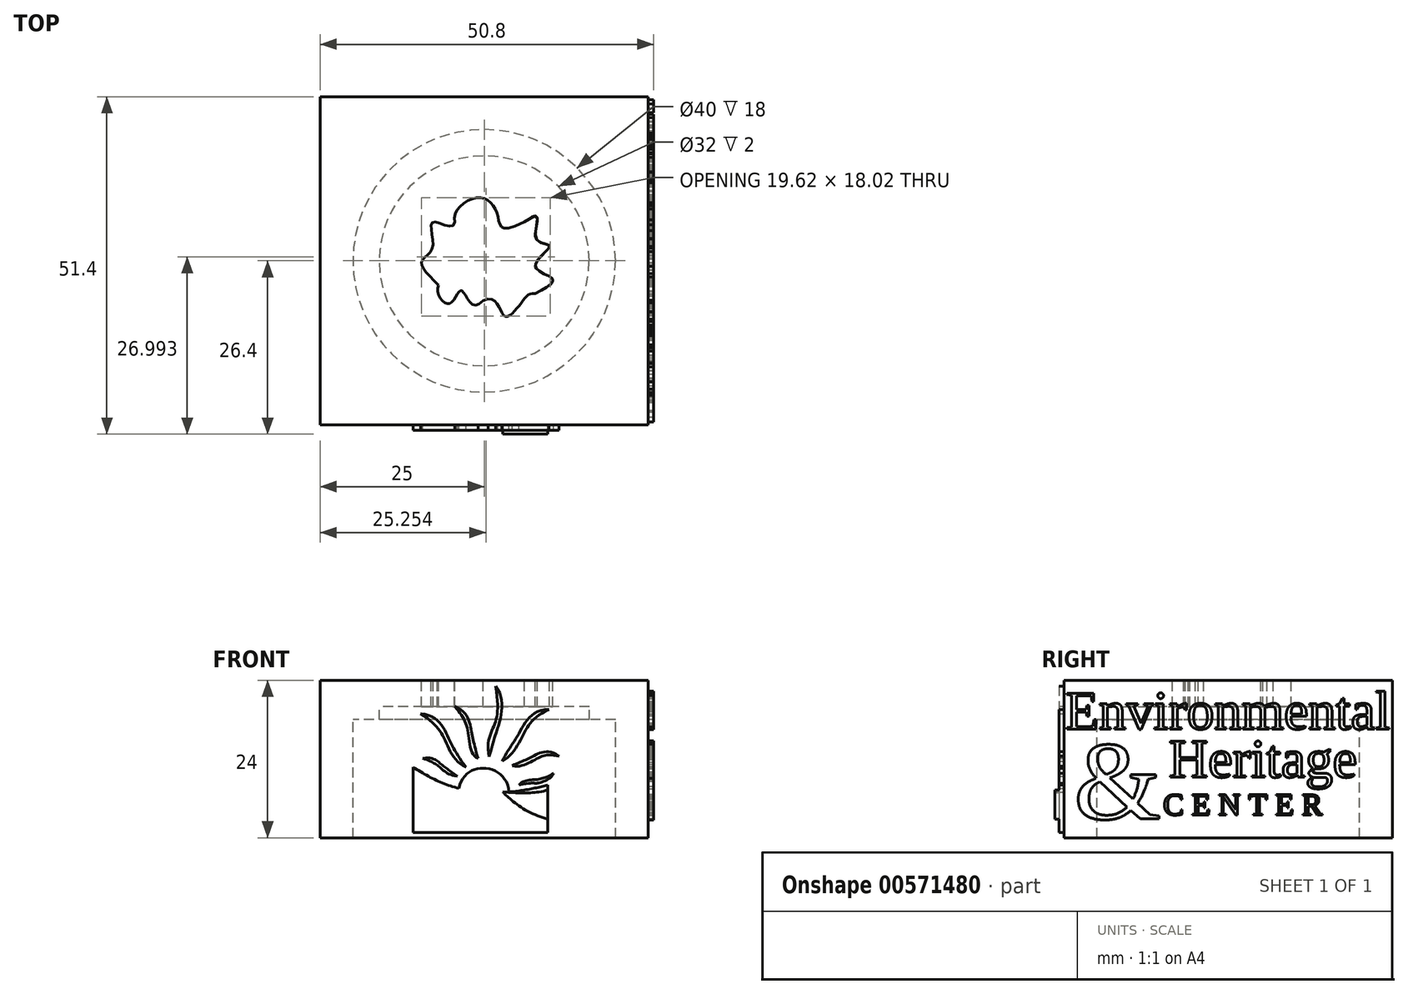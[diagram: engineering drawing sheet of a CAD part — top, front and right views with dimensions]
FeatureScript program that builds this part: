
annotation { "Feature Type Name" : "Feature", "Feature Type Description" : "" }
export const myFeature = defineFeature(function(context is Context, id is Id, definition is map)
    precondition{}
    {
        {
            var Q0;
            Q0=qCreatedBy(makeId("Top.planeOp"),FACE);
            var Q1;
            Q1=qBodyType(qCreatedBy(id+"F1",EDGE),BodyType.WIRE);
            cPlane(context, id + "F0", {"entities" : qUnion([Q0, Q1]), "cplaneType" : CPlaneType.OFFSET, "offset" : 12 * mm, "width" : 150 * mm, "height" : 150 * mm});
        }
        {
            var Q0;
            Q0=qCreatedBy(id+"F0.planeOp",FACE);
            var sketch = newSketch(context, id + "F1", { "sketchPlane" : qUnion([Q0])});
            skCircle(sketch, "E0", {"center": v(0, 0) * mm, "radius": 22 * mm});
            skCircle(sketch, "E1", {"center": v(0, 0) * mm, "radius": 20 * mm});
            skLineSegment(sketch, "E2.bottom", {"start": v(-25, 25) * mm, "end": v(25, 25) * mm});
            skLineSegment(sketch, "E2.top", {"start": v(-25, -25) * mm, "end": v(25, -25) * mm});
            skLineSegment(sketch, "E2.left", {"start": v(-25, 25) * mm, "end": v(-25, -25) * mm});
            skLineSegment(sketch, "E2.right", {"start": v(25, 25) * mm, "end": v(25, -25) * mm});
            skFitSpline(sketch, "E3", {"points": [v(6.14, 5.9) * mm, v(2.03, 7.03) * mm, v(-1.07, 9.6) * mm, v(-4.49, 5.9) * mm], "startDerivative": vector(-37.97, -19.2) * mm, "endDerivative": vector(4.73, -13.73) * mm});
            skFitSpline(sketch, "E4", {"points": [v(-4.49, 5.9) * mm, v(-7.75, 5.9) * mm, v(-7.85, 2.06) * mm, v(-9.5, -0.02) * mm, v(-6.95, -3.7) * mm], "startDerivative": vector(-0.77, -19.25) * mm, "endDerivative": vector(17.43, -16.5) * mm});
            skFitSpline(sketch, "E5", {"points": [v(-6.95, -3.7) * mm, v(-5.34, -6.54) * mm, v(-3.42, -4.56) * mm, v(-0.16, -6.05) * mm], "startDerivative": vector(-5.94, -10.16) * mm, "endDerivative": vector(15.66, 18.1) * mm});
            skFitSpline(sketch, "E6", {"points": [v(-0.16, -6.05) * mm, v(3.1, -8.4) * mm, v(5.82, -6.16) * mm, v(7.8, -4.99) * mm], "startDerivative": vector(18.56, 8.63) * mm, "endDerivative": vector(11.76, -0.42) * mm});
            skFitSpline(sketch, "E7", {"points": [v(7.8, -4.99) * mm, v(10.41, -2.8) * mm, v(7.8, -0.82) * mm, v(9.93, 2.28) * mm, v(7.8, 3.83) * mm, v(6.14, 5.9) * mm], "startDerivative": vector(20.8, 11.18) * mm, "endDerivative": vector(-51.3, -41.03) * mm});
            skSolve(sketch);
        }
        {
            var Q0;
            Q0=qCreatedBy(makeId("Top.planeOp"),FACE);
            cPlane(context, id + "F2", {"entities" : qUnion([Q0]), "cplaneType" : CPlaneType.OFFSET, "offset" : 8 * mm, "width" : 150 * mm, "height" : 150 * mm});
        }
        {
            var Q0;
            Q0=qCreatedBy(id+"F2.planeOp",FACE);
            var sketch = newSketch(context, id + "F3", { "sketchPlane" : qUnion([Q0])});
            skCircle(sketch, "E8", {"center": v(0, 0) * mm, "radius": 20 * mm});
            skCircle(sketch, "E9", {"center": v(0, 0) * mm, "radius": 16 * mm});
            skSolve(sketch);
        }
        {
            var Q0;
            Q0=makeQuery(id+"F1.imprint","IMPRINT",FACE,{"disambiguationData":[TD([[makeQuery(id+"F1.imprint","IMPRINT",EDGE,{"derivedFrom":sQuery(id+"F1.wireOp",EDGE,"E1")}),1.0]])]});
            extrude(context, id + "F4", {"entities" : qUnion([Q0]), "oppositeDirection" : true, "depth" : 4 * mm, "offsetDistance" : 25 * mm});
        }
        {
            var Q0;
            Q0=makeQuery(id+"F1.imprint","IMPRINT",FACE,{"disambiguationData":[TD([[makeQuery(id+"F1.imprint","IMPRINT",EDGE,{"derivedFrom":sQuery(id+"F1.wireOp",EDGE,"E0")}),1.0]])]});
            var Q1;
            Q1=makeQuery(id+"F1.imprint","IMPRINT",FACE,{"disambiguationData":[TD([[makeQuery(id+"F1.imprint","IMPRINT",EDGE,{"derivedFrom":sQuery(id+"F1.wireOp",EDGE,"E0")}),-1.0]])]});
            extrude(context, id + "F5", {"entities" : qUnion([Q0, Q1]), "operationType" : NewBodyOperationType.ADD, "oppositeDirection" : true, "depth" : 24 * mm, "offsetDistance" : 25 * mm});
        }
        {
            var Q0;
            Q0=makeQuery(id+"F3.imprint","IMPRINT",FACE,{"disambiguationData":[TD([[makeQuery(id+"F3.imprint","IMPRINT",EDGE,{"derivedFrom":sQuery(id+"F3.wireOp",EDGE,"E8")}),1.0]])]});
            extrude(context, id + "F6", {"entities" : qUnion([Q0]), "operationType" : NewBodyOperationType.ADD, "oppositeDirection" : true, "depth" : 2 * mm});
        }
        {
            var Q0;
            Q0=qCreatedBy(id+"F0.planeOp",FACE);
            var sketch = newSketch(context, id + "F7", { "sketchPlane" : qUnion([Q0])});
            skCircle(sketch, "E10", {"center": v(0, 0) * mm, "radius": 22.4 * mm});
            skSolve(sketch);
        }
        {
            var Q0;
            Q0=qSketchRegion(id+"F7",true);
            var Q1;
            Q1=qConstructionFilter(qBodyType(qCreatedBy(id+"F7",EDGE),BodyType.WIRE),ConstructionObject.NO);
            extrude(context, id + "F8", {"entities" : qUnion([Q0]), "bodyType" : ToolBodyType.SURFACE, "operationType" : NewBodyOperationType.ADD, "surfaceEntities" : qUnion([Q1]), "oppositeDirection" : true, "depth" : 24 * mm});
        }
        {
            var Q0;
            Q0=makeQuery(id+"F5.opExtrude","SWEPT_FACE",FACE,{"disambiguationData":[OSD([sQuery(id+"F1.wireOp",EDGE,"E2.right")])]});
            var sketch = newSketch(context, id + "F9", { "sketchPlane" : qUnion([Q0])});
            skText(sketch, "E11", { "text": "Environmental", "fontName": "Tinos-Regular.ttf"});
            skText(sketch, "E12", { "text": "Heritage", "fontName": "Tinos-Regular.ttf"});
            skText(sketch, "E13", { "text": "C E N T E R", "fontName": "Tinos-Regular.ttf"});
            skText(sketch, "E14", { "text": "&", "fontName": "Tinos-Regular.ttf"});
            const initialGuessF9  = {"E11": [-0.02481, 0.00457, 1, 0, 0.006], "E12": [-0.00905, -0.00277, 1, 0, 0.006], "E13": [-0.0099, -0.00853, 1, 0, 0.0034], "E14": [-0.0235, -0.00912, 1, 0, 0.0123]};
            skSetInitialGuess(sketch, initialGuessF9);
            skSolve(sketch);
        }
        {
            var Q0;
            Q0=qSketchRegion(id+"F9",true);
            var Q1;
            Q1=makeQuery(id+"F8.opExtrude","SWEPT_FACE",FACE,{"disambiguationData":[OSD([sQuery(id+"F7.wireOp",EDGE,"E10")])]});
            var Q2;
            Q2=makeQuery(id+"F5.opExtrude","SWEPT_FACE",FACE,{"disambiguationData":[OSD([sQuery(id+"F1.wireOp",EDGE,"E0")])]});
            extrude(context, id + "F10", {"entities" : qUnion([Q0]), "operationType" : NewBodyOperationType.ADD, "endBoundEntityFace" : qUnion([Q1]), "depth" : .8 * mm, "offsetDistance" : 25 * mm});
        }
        {
            var Q0;
            Q0=makeQuery(id+"F5.opExtrude","SWEPT_FACE",FACE,{"disambiguationData":[OSD([sQuery(id+"F1.wireOp",EDGE,"E2.top")])]});
            var sketch = newSketch(context, id + "F11", { "sketchPlane" : qUnion([Q0])});
            skFitSpline(sketch, "E15", {"points": [v(1.72, 11.1) * mm, v(2.15, 5) * mm, v(0.74, 0.35) * mm], "startDerivative": vector(9.25, -10.85) * mm, "endDerivative": vector(-6.86, -24.58) * mm});
            skFitSpline(sketch, "E16", {"points": [v(1.72, 11.1) * mm, v(1.41, 4.9) * mm, v(0.74, 0.35) * mm], "startDerivative": vector(3.34, -19.7) * mm, "endDerivative": vector(3.13, -13.42) * mm});
            skFitSpline(sketch, "E17", {"points": [v(-4.5, 8.04) * mm, v(-1.98, 4.33) * mm, v(-0.94, 0.08) * mm], "startDerivative": vector(12.14, -4.86) * mm, "endDerivative": vector(3.6, -12.42) * mm});
            skFitSpline(sketch, "E18", {"points": [v(-4.5, 8.04) * mm, v(-2.48, 4.19) * mm, v(-0.94, 0.08) * mm], "startDerivative": vector(7.17, -8.39) * mm, "endDerivative": vector(7.68, -2.86) * mm});
            skFitSpline(sketch, "E19", {"points": [v(-9.7, 6.92) * mm, v(-5.5, 3.33) * mm, v(-2.77, -1.2) * mm], "startDerivative": vector(15.8, -1.39) * mm, "endDerivative": vector(8.45, -10.79) * mm});
            skFitSpline(sketch, "E20", {"points": [v(-9.7, 6.92) * mm, v(-6.04, 3) * mm, v(-2.77, -1.2) * mm], "startDerivative": vector(12.7, -8.12) * mm, "endDerivative": vector(11.68, -4.6) * mm});
            skFitSpline(sketch, "E21", {"points": [v(9.9, 7.54) * mm, v(5.27, 3.86) * mm, v(2.73, -0.34) * mm], "startDerivative": vector(-16.28, 0.17) * mm, "endDerivative": vector(-5.04, -10.45) * mm});
            skFitSpline(sketch, "E22", {"points": [v(9.9, 7.54) * mm, v(6.03, 3.9) * mm, v(2.73, -0.34) * mm], "startDerivative": vector(-14.08, -6.51) * mm, "endDerivative": vector(-10.47, -5.32) * mm});
            skFitSpline(sketch, "E23", {"points": [v(4.27, -1.02) * mm, v(7.3, 0.36) * mm, v(11.36, 0.45) * mm], "startDerivative": vector(8.09, 3.76) * mm, "endDerivative": vector(9.5, -7.16) * mm});
            skFitSpline(sketch, "E24", {"points": [v(4.27, -1.02) * mm, v(8.42, 0.27) * mm, v(11.36, 0.45) * mm], "startDerivative": vector(8.44, -2.27) * mm, "endDerivative": vector(8.91, -1.55) * mm});
            skFitSpline(sketch, "E25", {"points": [v(5.29, -3.98) * mm, v(8.06, -3.11) * mm, v(10.55, -2.2) * mm], "startDerivative": vector(4.54, 5.24) * mm, "endDerivative": vector(4.83, 3.04) * mm});
            skFitSpline(sketch, "E26", {"points": [v(5.29, -3.98) * mm, v(8.07, -3.68) * mm, v(10.55, -2.2) * mm], "startDerivative": vector(14.94, 3.04) * mm, "endDerivative": vector(2.67, 5.86) * mm});
            skFitSpline(sketch, "E27", {"points": [v(-9.37, 0.12) * mm, v(-6.47, -0.87) * mm, v(-4.11, -2.63) * mm], "startDerivative": vector(10.1, 1.37) * mm, "endDerivative": vector(5.45, -4.16) * mm});
            skFitSpline(sketch, "E28", {"points": [v(-9.37, 0.12) * mm, v(-6.93, -1.1) * mm, v(-4.11, -2.63) * mm], "startDerivative": vector(7.6, -2.83) * mm, "endDerivative": vector(8.5, -0.9) * mm});
            skFitSpline(sketch, "E29", {"points": [v(-10.86, -1.23) * mm, v(-6.06, -3.79) * mm, v(-1, -4.96) * mm], "startDerivative": vector(9.3, -5.74) * mm, "endDerivative": vector(10.6, -1.22) * mm});
            skFitSpline(sketch, "E30", {"points": [v(-1, -4.96) * mm, v(3.57, -8.3) * mm, v(9.7, -10.31) * mm], "startDerivative": vector(8.63, -8.7) * mm, "endDerivative": vector(13.46, -2.5) * mm});
            skFitSpline(sketch, "E31", {"points": [v(-0.18, -5.02) * mm, v(4.02, -7.88) * mm, v(9.7, -9.8) * mm], "startDerivative": vector(7.75, -7.13) * mm, "endDerivative": vector(11.6, -2.38) * mm});
            skFitSpline(sketch, "E32", {"points": [v(-0.18, -5.02) * mm, v(5.2, -4.87) * mm, v(9.7, -3.95) * mm], "startDerivative": vector(11.8, -0.67) * mm, "endDerivative": vector(9.04, 2.33) * mm});
            skFitSpline(sketch, "E33", {"points": [v(-10.86, -8.25) * mm, v(-3.26, -7.54) * mm, v(5.18, -11.18) * mm], "startDerivative": vector(16.62, 9.24) * mm, "endDerivative": vector(16.34, -9.64) * mm});
            skFitSpline(sketch, "E34", {"points": [v(-10.86, -8.96) * mm, v(-3.26, -8.11) * mm, v(4.28, -11.18) * mm], "startDerivative": vector(16.47, 11.33) * mm, "endDerivative": vector(14.69, -7.9) * mm});
            skLineSegment(sketch, "E35", {"start": v(-10.86, -1.23) * mm, "end": v(-10.86, -11.18) * mm});
            skLineSegment(sketch, "E36", {"start": v(-10.86, -11.18) * mm, "end": v(9.7, -11.18) * mm});
            skLineSegment(sketch, "E37", {"start": v(9.7, -3.95) * mm, "end": v(9.7, -11.18) * mm});
            skFitSpline(sketch, "E38", {"points": [v(-3.88, -4.46) * mm, v(0, -1.4) * mm, v(3.78, -5.02) * mm], "startDerivative": vector(3, 13.25) * mm, "endDerivative": vector(0.81, -13.52) * mm});
            skSolve(sketch);
        }
        {
            var Q0;
            Q0=qSketchRegion(id+"F11",true);
            var Q1;
            Q1=makeQuery(id+"F8.opExtrude","SWEPT_FACE",FACE,{"disambiguationData":[OSD([sQuery(id+"F7.wireOp",EDGE,"E10")])]});
            var Q2;
            {var subQ1=sQuery(id+"F1.wireOp",EDGE,"E0");Q2=makeQuery(id+"F10.boolean.opBoolean","SPLIT",FACE,{"disambiguationData":[TD([makeQuery(id+"F10.opExtrude","SWEPT_FACE",FACE,{"disambiguationData":[OSD([sQuery(id+"F9.wireOp",EDGE,"E11.sketch_text.stroke-0")])]})])],"derivedFrom":makeQuery(id+"F5.opExtrude","SWEPT_FACE",FACE,{"disambiguationData":[OSD([subQ1])]})});}
            extrude(context, id + "F12", {"entities" : qUnion([Q0]), "operationType" : NewBodyOperationType.ADD, "depth" : .8 * mm, "endBoundEntityFace" : qUnion([Q1]), "offsetDistance" : 25 * mm});
        }
        {
            var Q0;
            Q0=makeQuery(id+"F12.opExtrude","CAP_FACE",FACE,{"disambiguationData":[OSD([sQuery(id+"F11.wireOp",EDGE,"E29"),sQuery(id+"F11.wireOp",EDGE,"E32"),sQuery(id+"F11.wireOp",EDGE,"E35"),sQuery(id+"F11.wireOp",EDGE,"E36"),sQuery(id+"F11.wireOp",EDGE,"E37"),sQuery(id+"F11.wireOp",EDGE,"E38")])],"isStart":false});
            var sketch = newSketch(context, id + "F13", { "sketchPlane" : qUnion([Q0])});
            skFitSpline(sketch, "E39.0", {"points": [v(-7.86, -8.25) * mm, v(-5.22, -6.79) * mm, v(-0.09, -7.06) * mm, v(5.33, -9.5) * mm, v(8.18, -11.18) * mm]});
            skLineSegment(sketch, "E39.1", {"start": v(-10.86, -1.23) * mm, "end": v(-10.86, -8.25) * mm});
            skFitSpline(sketch, "E39.2", {"points": [v(-7.86, -1.23) * mm, v(-6.3, -2.2) * mm, v(-3.18, -4.07) * mm, v(0.26, -4.76) * mm, v(2, -4.96) * mm]});
            skFitSpline(sketch, "E39.3", {"points": [v(2, -4.96) * mm, v(3.4, -6.36) * mm, v(6.48, -8.59) * mm, v(10.38, -9.88) * mm, v(12.7, -10.31) * mm]});
            skFitSpline(sketch, "E39.4", {"points": [v(2.82, -5.02) * mm, v(4.06, -6.16) * mm, v(6.94, -8.13) * mm, v(10.69, -9.39) * mm, v(12.7, -9.8) * mm]});
            skFitSpline(sketch, "E39.5", {"points": [v(2.82, -5.02) * mm, v(4.86, -5.14) * mm, v(8.1, -5.05) * mm, v(11.25, -4.32) * mm, v(12.7, -3.95) * mm]});
            skLineSegment(sketch, "E39.6", {"start": v(9.7, -3.95) * mm, "end": v(9.7, -11.18) * mm});
            skLineSegment(sketch, "E39.7", {"start": v(-10.86, -11.18) * mm, "end": v(4.28, -11.18) * mm});
            skFitSpline(sketch, "E39.8", {"points": [v(-7.86, -8.96) * mm, v(-5.16, -7.1) * mm, v(-0.18, -7.8) * mm, v(4.8, -9.84) * mm, v(7.28, -11.18) * mm]});
            skLineSegment(sketch, "E40.trimOffspring", {"start": v(-10.86, -8.96) * mm, "end": v(-10.86, -11.18) * mm});
            skLineSegment(sketch, "E41.trimOffspring", {"start": v(5.18, -11.18) * mm, "end": v(9.7, -11.18) * mm});
            skSolve(sketch);
        }
        {
            var Q0;
            Q0=qSketchRegion(id+"F13",true);
            var Q1;
            Q1=makeQuery(id+"FNsWkgsrXxMfTFs_2.opExtrude","SWEPT_FACE",FACE,{"disambiguationData":[OSD([sQuery(id+"Fo9w5D1ibmldVsS_2.wireOp",EDGE,"mGLLwlgu-EK9b-grjT-Pw0f-xcvj3JAOEqAF")])]});
            var Q2;
            Q2=makeQuery(id+"F12.opExtrude","CAP_FACE",FACE,{"disambiguationData":[OSD([sQuery(id+"F7.wireOp",EDGE,"E10")]),OD(7.0)],"isStart":false});
            extrude(context, id + "F14", {"entities" : qUnion([Q0]), "operationType" : NewBodyOperationType.ADD, "depth" : .6 * mm, "endBoundEntityFace" : qUnion([Q1]), "offsetDistance" : 25 * mm});
        }
    });
